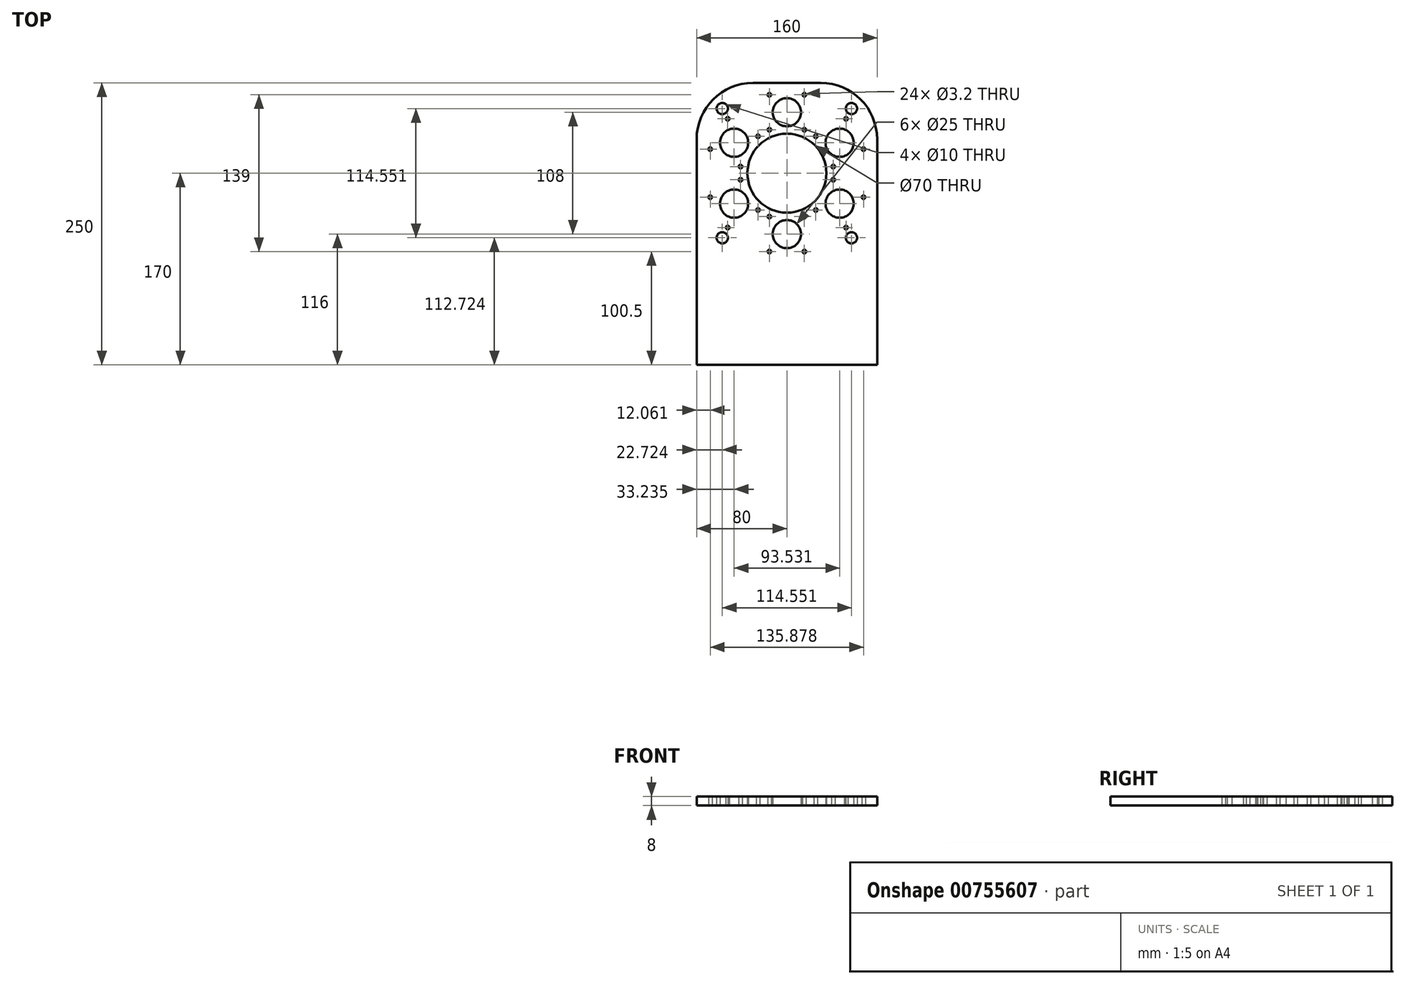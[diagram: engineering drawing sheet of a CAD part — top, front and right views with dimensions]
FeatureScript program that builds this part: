
annotation { "Feature Type Name" : "Feature", "Feature Type Description" : "" }
export const myFeature = defineFeature(function(context is Context, id is Id, definition is map)
    precondition{}
    {
        {
            var Q0;
            Q0=qCreatedBy(makeId("Top.planeOp"),FACE);
            var sketch = newSketch(context, id + "F0", { "sketchPlane" : qUnion([Q0])});
            skLineSegment(sketch, "E0.bottom", {"start": v(-80, 80) * mm, "end": v(80, 80) * mm});
            skLineSegment(sketch, "E0.top", {"start": v(-80, -170) * mm, "end": v(80, -170) * mm});
            skLineSegment(sketch, "E0.left", {"start": v(-80, 80) * mm, "end": v(-80, -170) * mm});
            skLineSegment(sketch, "E0.right", {"start": v(80, 80) * mm, "end": v(80, -170) * mm});
            skLineSegment(sketch, "E1", {"start": v(0, 80) * mm, "end": v(0, 0) * mm, "construction": true});
            skSolve(sketch);
        }
        {
            var Q0;
            Q0 = qSketchRegion(id + "F0", true);
            extrude(context, id + "F1", {"entities" : qUnion([Q0]), "depth" : 8 * mm, "offsetDistance" : 25 * mm});
        }
        {
            var Q0;
            Q0=qCreatedBy(makeId("Top.planeOp"),FACE);
            var sketch = newSketch(context, id + "F2", { "sketchPlane" : qUnion([Q0])});
            skLineSegment(sketch, "E2.bottom", {"start": v(-15.5, 69.5) * mm, "end": v(15.5, 69.5) * mm, "construction": true});
            skLineSegment(sketch, "E2.top", {"start": v(-15.5, 38.5) * mm, "end": v(15.5, 38.5) * mm, "construction": true});
            skLineSegment(sketch, "E2.left", {"start": v(-15.5, 69.5) * mm, "end": v(-15.5, 38.5) * mm, "construction": true});
            skLineSegment(sketch, "E2.right", {"start": v(15.5, 69.5) * mm, "end": v(15.5, 38.5) * mm, "construction": true});
            skCircle(sketch, "E3", {"center": v(0, 0) * mm, "radius": 35 * mm});
            skLineSegment(sketch, "E4", {"start": v(0, 38.5) * mm, "end": v(0, 0) * mm, "construction": true});
            skLineSegment(sketch, "E5", {"start": v(15.5, 54) * mm, "end": v(-15.5, 54) * mm, "construction": true});
            skCircle(sketch, "E6", {"center": v(-15.5, 69.5) * mm, "radius": 1.6 * mm});
            skCircle(sketch, "E7", {"center": v(15.5, 69.5) * mm, "radius": 1.6 * mm});
            skCircle(sketch, "E8", {"center": v(15.5, 38.5) * mm, "radius": 1.6 * mm});
            skCircle(sketch, "E9", {"center": v(-15.5, 38.5) * mm, "radius": 1.6 * mm});
            skCircle(sketch, "E10", {"center": v(0, 54) * mm, "radius": 12.5 * mm});
            skCircle(sketch, "E11.1.0", {"center": v(-67.94, 21.33) * mm, "radius": 1.6 * mm});
            skCircle(sketch, "E11.1.1", {"center": v(-41.1, 5.83) * mm, "radius": 1.6 * mm});
            skCircle(sketch, "E11.1.2", {"center": v(-25.6, 32.67) * mm, "radius": 1.6 * mm});
            skCircle(sketch, "E11.1.3", {"center": v(-52.44, 48.17) * mm, "radius": 1.6 * mm});
            skCircle(sketch, "E11.1.4", {"center": v(-46.77, 27) * mm, "radius": 12.5 * mm});
            skCircle(sketch, "E11.2.0", {"center": v(-52.44, -48.17) * mm, "radius": 1.6 * mm});
            skCircle(sketch, "E11.2.1", {"center": v(-25.6, -32.67) * mm, "radius": 1.6 * mm});
            skCircle(sketch, "E11.2.2", {"center": v(-41.1, -5.83) * mm, "radius": 1.6 * mm});
            skCircle(sketch, "E11.2.3", {"center": v(-67.94, -21.33) * mm, "radius": 1.6 * mm});
            skCircle(sketch, "E11.2.4", {"center": v(-46.77, -27) * mm, "radius": 12.5 * mm});
            skCircle(sketch, "E11.3.0", {"center": v(15.5, -69.5) * mm, "radius": 1.6 * mm});
            skCircle(sketch, "E11.3.1", {"center": v(15.5, -38.5) * mm, "radius": 1.6 * mm});
            skCircle(sketch, "E11.3.2", {"center": v(-15.5, -38.5) * mm, "radius": 1.6 * mm});
            skCircle(sketch, "E11.3.3", {"center": v(-15.5, -69.5) * mm, "radius": 1.6 * mm});
            skCircle(sketch, "E11.3.4", {"center": v(0, -54) * mm, "radius": 12.5 * mm});
            skCircle(sketch, "E11.4.0", {"center": v(67.94, -21.33) * mm, "radius": 1.6 * mm});
            skCircle(sketch, "E11.4.1", {"center": v(41.1, -5.83) * mm, "radius": 1.6 * mm});
            skCircle(sketch, "E11.4.2", {"center": v(25.6, -32.67) * mm, "radius": 1.6 * mm});
            skCircle(sketch, "E11.4.3", {"center": v(52.44, -48.17) * mm, "radius": 1.6 * mm});
            skCircle(sketch, "E11.4.4", {"center": v(46.77, -27) * mm, "radius": 12.5 * mm});
            skCircle(sketch, "E11.5.0", {"center": v(52.44, 48.17) * mm, "radius": 1.6 * mm});
            skCircle(sketch, "E11.5.1", {"center": v(25.6, 32.67) * mm, "radius": 1.6 * mm});
            skCircle(sketch, "E11.5.2", {"center": v(41.1, 5.83) * mm, "radius": 1.6 * mm});
            skCircle(sketch, "E11.5.3", {"center": v(67.94, 21.33) * mm, "radius": 1.6 * mm});
            skCircle(sketch, "E11.5.4", {"center": v(46.77, 27) * mm, "radius": 12.5 * mm});
            skSolve(sketch);
        }
        {
            var Q0;
            Q0 = qSketchRegion(id + "F2", true);
            extrude(context, id + "F3", {"entities" : qUnion([Q0]), "operationType" : NewBodyOperationType.REMOVE, "endBound" : BoundingType.THROUGH_ALL, "depth" : 25 * mm, "offsetDistance" : 25 * mm});
        }
        {
            var Q0;
            Q0=qCreatedBy(makeId("Top.planeOp"),FACE);
            var sketch = newSketch(context, id + "F4", { "sketchPlane" : qUnion([Q0])});
            skLineSegment(sketch, "E12", {"start": v(0, 0) * mm, "end": v(57.28, 57.28) * mm, "construction": true});
            skCircle(sketch, "E13", {"center": v(57.28, 57.28) * mm, "radius": 5 * mm});
            skCircle(sketch, "E14.1.0", {"center": v(-57.28, 57.28) * mm, "radius": 5 * mm});
            skCircle(sketch, "E14.2.0", {"center": v(-57.28, -57.28) * mm, "radius": 5 * mm});
            skCircle(sketch, "E14.3.0", {"center": v(57.28, -57.28) * mm, "radius": 5 * mm});
            skPoint(sketch, "E14.center", {"position": v(0, 0) * mm});
            skSolve(sketch);
        }
        {
            var Q0;
            Q0 = qSketchRegion(id + "F4", true);
            extrude(context, id + "F5", {"entities" : qUnion([Q0]), "operationType" : NewBodyOperationType.REMOVE, "endBound" : BoundingType.THROUGH_ALL, "depth" : 25 * mm, "offsetDistance" : 25 * mm});
        }
        {
            var Q0;
            Q0=makeQuery(id+"F1.opExtrude","SWEPT_EDGE",EDGE,{"disambiguationData":[OSD([sQuery(id+"F0.wireOp",EDGE,"E0.bottom"),sQuery(id+"F0.wireOp",EDGE,"E0.right")])]});
            var Q1;
            Q1=makeQuery(id+"F1.opExtrude","SWEPT_EDGE",EDGE,{"disambiguationData":[OSD([sQuery(id+"F0.wireOp",EDGE,"E0.bottom"),sQuery(id+"F0.wireOp",EDGE,"E0.left")])]});
            fillet(context, id + "F6", {"entities" : qUnion([Q0, Q1]), "radius" : 50 * mm, "tangentPropagation" : true, "allowEdgeOverflow" : false});
        }
    });
